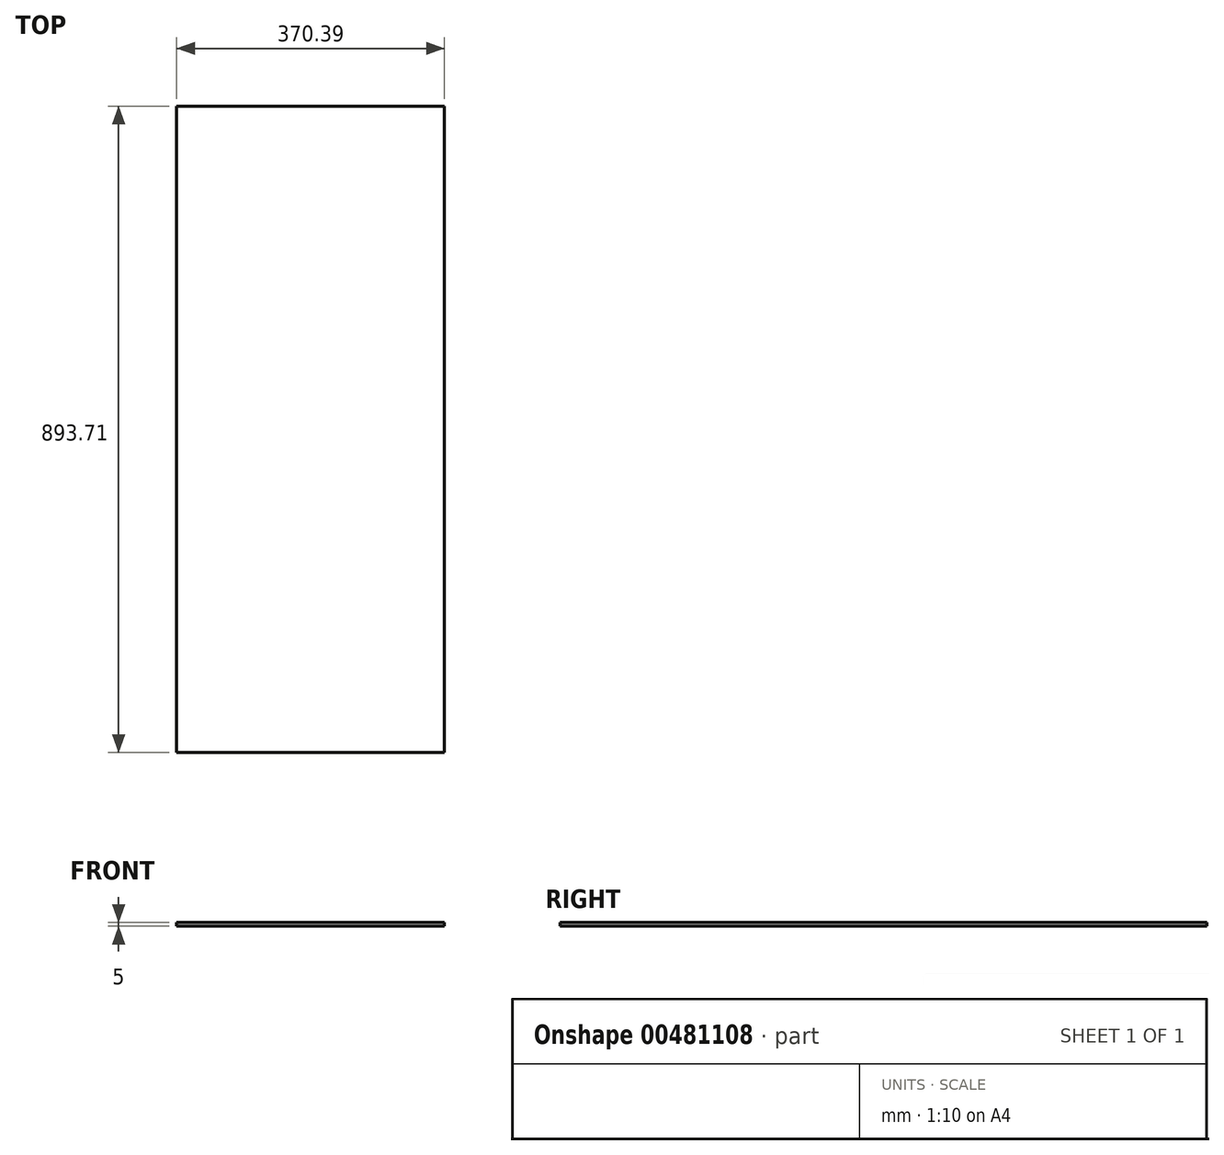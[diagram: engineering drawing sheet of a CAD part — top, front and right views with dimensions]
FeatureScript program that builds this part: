
annotation { "Feature Type Name" : "Feature", "Feature Type Description" : "" }
export const myFeature = defineFeature(function(context is Context, id is Id, definition is map)
    precondition{}
    {
        {
            var Q0;
            Q0=qCreatedBy(makeId("Top.planeOp"),FACE);
            var sketch = newSketch(context, id + "F0", { "sketchPlane" : qUnion([Q0])});
            skLineSegment(sketch, "E0.bottom", {"start": v(-158.33, -328.26) * mm, "end": v(212.06, -328.26) * mm});
            skLineSegment(sketch, "E0.top", {"start": v(-158.33, 565.45) * mm, "end": v(212.06, 565.45) * mm});
            skLineSegment(sketch, "E0.left", {"start": v(-158.33, -328.26) * mm, "end": v(-158.33, 565.45) * mm});
            skLineSegment(sketch, "E0.right", {"start": v(212.06, -328.26) * mm, "end": v(212.06, 565.45) * mm});
            skSolve(sketch);
        }
        {
            var Q0;
            Q0 = qSketchRegion(id + "F0", true);
            extrude(context, id + "F1", {"entities" : qUnion([Q0]), "depth" : 5 * mm, "offsetDistance" : 25 * mm});
        }
    });
